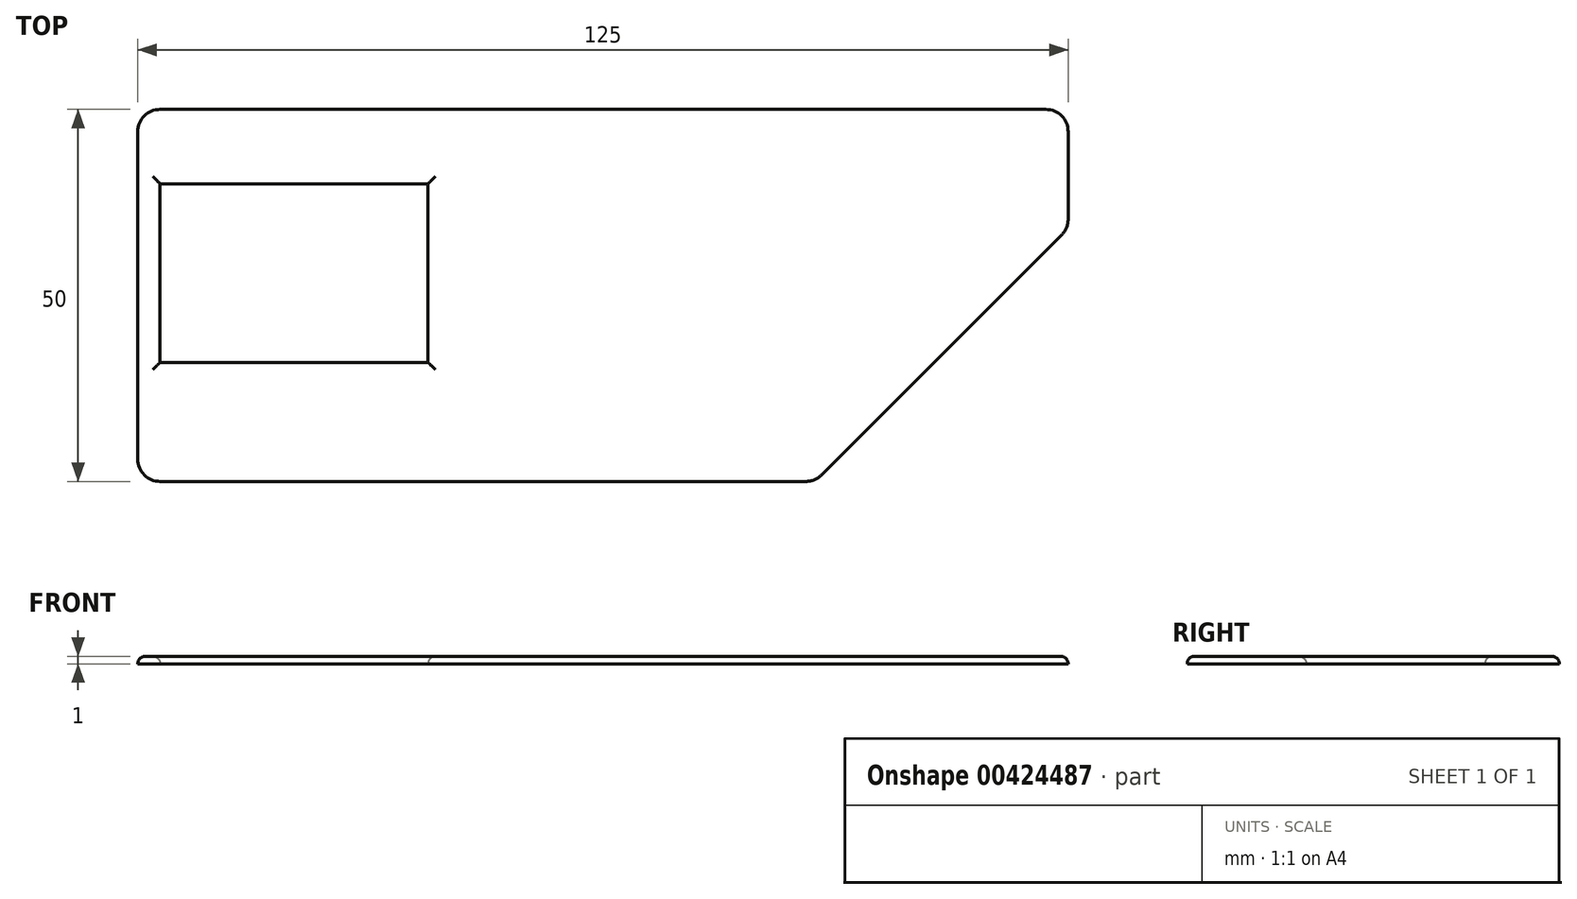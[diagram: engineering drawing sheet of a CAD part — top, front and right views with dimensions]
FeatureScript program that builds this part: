
annotation { "Feature Type Name" : "Feature", "Feature Type Description" : "" }
export const myFeature = defineFeature(function(context is Context, id is Id, definition is map)
    precondition{}
    {
        {
            var Q0;
            Q0=qCreatedBy(makeId("Top.planeOp"),FACE);
            var sketch = newSketch(context, id + "F0", { "sketchPlane" : qUnion([Q0])});
            skLineSegment(sketch, "E0.bottom", {"start": v(62.5, 25) * mm, "end": v(-62.5, 25) * mm});
            skLineSegment(sketch, "E0.top", {"start": v(28.5, -25) * mm, "end": v(-62.5, -25) * mm});
            skLineSegment(sketch, "E0.left", {"start": v(62.5, 25) * mm, "end": v(62.5, 9) * mm});
            skLineSegment(sketch, "E0.right", {"start": v(-62.5, 25) * mm, "end": v(-62.5, -25) * mm});
            skPoint(sketch, "E0.middle", {"position": v(0, 0) * mm});
            skLineSegment(sketch, "E1", {"start": v(28.5, -25) * mm, "end": v(62.5, 9) * mm});
            skPoint(sketch, "E2.orphan", {"position": v(62.5, -25) * mm});
            skSolve(sketch);
        }
        {
            var Q0;
            Q0=makeQuery(id+"F0.imprint","IMPRINT",FACE,{"disambiguationData":[TD([[makeQuery(id+"F0.imprint","IMPRINT",EDGE,{"derivedFrom":sQuery(id+"F0.wireOp",EDGE,"E0.bottom")}),1.0]])]});
            extrude(context, id + "F1", {"entities" : qUnion([Q0]), "depth" : 1 * mm});
        }
        {
            var Q0;
            Q0=makeQuery(id+"F1.opExtrude","CAP_FACE",FACE,{"disambiguationData":[OSD([sQuery(id+"F0.wireOp",EDGE,"E0.bottom"),sQuery(id+"F0.wireOp",EDGE,"E0.top"),sQuery(id+"F0.wireOp",EDGE,"E0.left"),sQuery(id+"F0.wireOp",EDGE,"E0.right")])],"isStart":false});
            var sketch = newSketch(context, id + "F2", { "sketchPlane" : qUnion([Q0])});
            skLineSegment(sketch, "E3.bottom", {"start": v(-23.5, 15) * mm, "end": v(-59.5, 15) * mm});
            skLineSegment(sketch, "E3.top", {"start": v(-23.5, -9) * mm, "end": v(-59.5, -9) * mm});
            skLineSegment(sketch, "E3.left", {"start": v(-23.5, 15) * mm, "end": v(-23.5, -9) * mm});
            skLineSegment(sketch, "E3.right", {"start": v(-59.5, 15) * mm, "end": v(-59.5, -9) * mm});
            skPoint(sketch, "E3.middle", {"position": v(-41.5, 3) * mm});
            skSolve(sketch);
        }
        {
            var Q0;
            Q0=makeQuery(id+"F2.imprint","IMPRINT",FACE,{"disambiguationData":[TD([[makeQuery(id+"F2.imprint","IMPRINT",EDGE,{"derivedFrom":sQuery(id+"F2.wireOp",EDGE,"E3.bottom")}),1.0]])]});
            extrude(context, id + "F3", {"entities" : qUnion([Q0]), "operationType" : NewBodyOperationType.REMOVE, "oppositeDirection" : true, "depth" : 25 * mm});
        }
        {
            var Q0;
            Q0=makeQuery(id+"F50R3ssp6eMTp0L_1.opExtrude","SWEPT_EDGE",EDGE,{"disambiguationData":[OSD([sQuery(id+"FhmRn0rDpILzKye_1.wireOp",EDGE,"hX9DthlI-q3t4-7Svd-GVoW-braHI3PCwNRM.bottom"),sQuery(id+"FhmRn0rDpILzKye_1.wireOp",EDGE,"hX9DthlI-q3t4-7Svd-GVoW-braHI3PCwNRM.right")])]});
            var Q1;
            Q1=makeQuery(id+"F1.opExtrude","SWEPT_EDGE",EDGE,{"disambiguationData":[OSD([sQuery(id+"F0.wireOp",EDGE,"E0.bottom"),sQuery(id+"F0.wireOp",EDGE,"E0.right")])]});
            var Q2;
            Q2=makeQuery(id+"F1.opExtrude","SWEPT_EDGE",EDGE,{"disambiguationData":[OSD([sQuery(id+"F0.wireOp",EDGE,"E0.top"),sQuery(id+"F0.wireOp",EDGE,"E0.right")])]});
            var Q3;
            Q3=makeQuery(id+"F50R3ssp6eMTp0L_1.opExtrude","SWEPT_EDGE",EDGE,{"disambiguationData":[OSD([sQuery(id+"FhmRn0rDpILzKye_1.wireOp",EDGE,"hX9DthlI-q3t4-7Svd-GVoW-braHI3PCwNRM.bottom"),sQuery(id+"FhmRn0rDpILzKye_1.wireOp",EDGE,"26wFQUay-XCHL-feOY-vWvD-cAKmWUWOlsiB")])]});
            var Q4;
            Q4=makeQuery(id+"F50R3ssp6eMTp0L_1.opExtrude","SWEPT_EDGE",EDGE,{"disambiguationData":[OSD([sQuery(id+"FhmRn0rDpILzKye_1.wireOp",EDGE,"hX9DthlI-q3t4-7Svd-GVoW-braHI3PCwNRM.top"),sQuery(id+"FhmRn0rDpILzKye_1.wireOp",EDGE,"hX9DthlI-q3t4-7Svd-GVoW-braHI3PCwNRM.right")])]});
            var Q5;
            Q5=makeQuery(id+"F1.opExtrude","SWEPT_EDGE",EDGE,{"disambiguationData":[OSD([sQuery(id+"F0.wireOp",EDGE,"E0.bottom"),sQuery(id+"F0.wireOp",EDGE,"E0.left")])]});
            var Q6;
            Q6=makeQuery(id+"F50R3ssp6eMTp0L_1.opExtrude","SWEPT_EDGE",EDGE,{"disambiguationData":[OSD([sQuery(id+"FhmRn0rDpILzKye_1.wireOp",EDGE,"hX9DthlI-q3t4-7Svd-GVoW-braHI3PCwNRM.top"),sQuery(id+"FhmRn0rDpILzKye_1.wireOp",EDGE,"hX9DthlI-q3t4-7Svd-GVoW-braHI3PCwNRM.left")])]});
            var Q7;
            Q7=makeQuery(id+"F1.opExtrude","SWEPT_EDGE",EDGE,{"disambiguationData":[OSD([sQuery(id+"F0.wireOp",EDGE,"E0.top"),sQuery(id+"F0.wireOp",EDGE,"E1")])]});
            var Q8;
            Q8=makeQuery(id+"F50R3ssp6eMTp0L_1.opExtrude","SWEPT_EDGE",EDGE,{"disambiguationData":[OSD([sQuery(id+"FhmRn0rDpILzKye_1.wireOp",EDGE,"hX9DthlI-q3t4-7Svd-GVoW-braHI3PCwNRM.left"),sQuery(id+"FhmRn0rDpILzKye_1.wireOp",EDGE,"26wFQUay-XCHL-feOY-vWvD-cAKmWUWOlsiB")])]});
            var Q9;
            Q9=makeQuery(id+"F1.opExtrude","SWEPT_EDGE",EDGE,{"disambiguationData":[OSD([sQuery(id+"F0.wireOp",EDGE,"E0.left"),sQuery(id+"F0.wireOp",EDGE,"E1")])]});
            fillet(context, id + "F4", {"entities" : qUnion([Q0, Q1, Q2, Q3, Q4, Q5, Q6, Q7, Q8, Q9]), "radius" : 3 * mm, "tangentPropagation" : true, "allowEdgeOverflow" : false});
        }
        {
            var Q0;
            Q0=makeQuery(id+"F1.opExtrude","CAP_FACE",FACE,{"disambiguationData":[OSD([sQuery(id+"F0.wireOp",EDGE,"E0.bottom"),sQuery(id+"F0.wireOp",EDGE,"E0.top"),sQuery(id+"F0.wireOp",EDGE,"E0.left"),sQuery(id+"F0.wireOp",EDGE,"E0.right"),sQuery(id+"F0.wireOp",EDGE,"E1")])],"isStart":false});
            fillet(context, id + "F5", {"entities" : qUnion([Q0]), "radius" : 1 * mm, "tangentPropagation" : true, "allowEdgeOverflow" : false});
        }
    });
